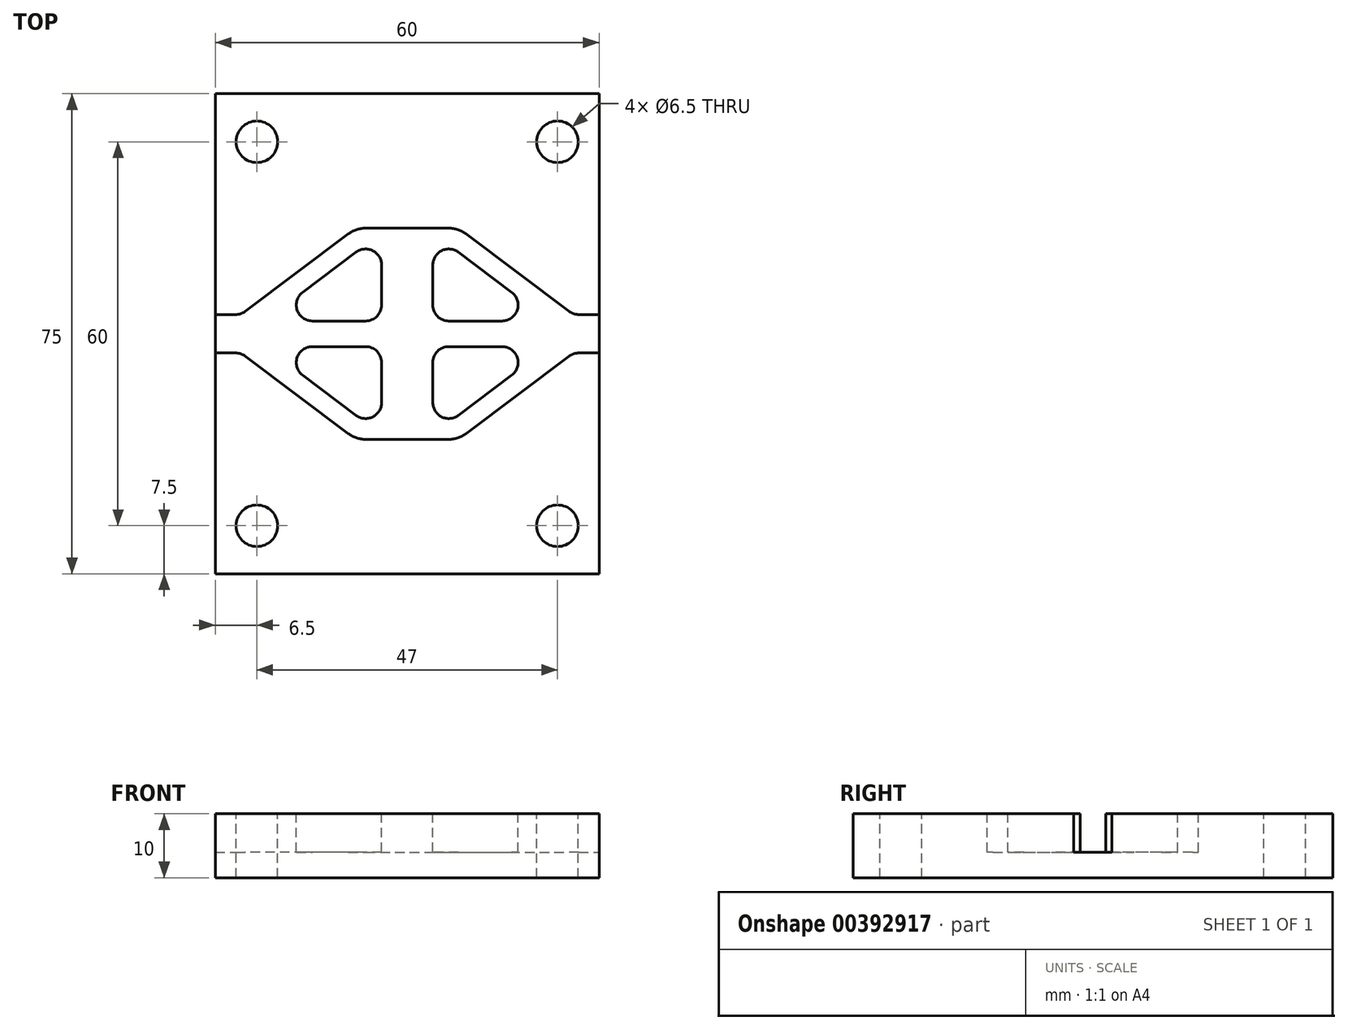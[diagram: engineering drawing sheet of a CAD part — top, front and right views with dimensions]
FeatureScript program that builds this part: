
annotation { "Feature Type Name" : "Feature", "Feature Type Description" : "" }
export const myFeature = defineFeature(function(context is Context, id is Id, definition is map)
    precondition{}
    {
        {
            var Q0;
            Q0=qCreatedBy(makeId("Top.planeOp"),FACE);
            var sketch = newSketch(context, id + "F0", { "sketchPlane" : qUnion([Q0])});
            skLineSegment(sketch, "E0.bottom", {"start": v(-30, 37.5) * mm, "end": v(30, 37.5) * mm});
            skLineSegment(sketch, "E0.top", {"start": v(-30, -37.5) * mm, "end": v(30, -37.5) * mm});
            skLineSegment(sketch, "E0.left", {"start": v(-30, 37.5) * mm, "end": v(-30, -37.5) * mm});
            skLineSegment(sketch, "E0.right", {"start": v(30, 37.5) * mm, "end": v(30, -37.5) * mm});
            skLineSegment(sketch, "E1", {"start": v(0, 76.83) * mm, "end": v(0, -62.83) * mm, "construction": true});
            skLineSegment(sketch, "E2", {"start": v(-62.67, 0) * mm, "end": v(69.33, 0) * mm, "construction": true});
            skLineSegment(sketch, "E3.bottom", {"start": v(-23.5, 30) * mm, "end": v(23.5, 30) * mm, "construction": true});
            skLineSegment(sketch, "E3.top", {"start": v(-23.5, -30) * mm, "end": v(23.5, -30) * mm, "construction": true});
            skLineSegment(sketch, "E3.left", {"start": v(-23.5, 30) * mm, "end": v(-23.5, -30) * mm, "construction": true});
            skLineSegment(sketch, "E3.right", {"start": v(23.5, 30) * mm, "end": v(23.5, -30) * mm, "construction": true});
            skSolve(sketch);
        }
        {
            var Q0;
            Q0=makeQuery(id+"F0.imprint","IMPRINT",FACE,{"disambiguationData":[TD([[makeQuery(id+"F0.imprint","IMPRINT",EDGE,{"derivedFrom":sQuery(id+"F0.wireOp",EDGE,"E0.bottom")}),-1.0]])]});
            extrude(context, id + "F1", {"entities" : qUnion([Q0]), "oppositeDirection" : true, "depth" : 10 * mm});
        }
        {
            var Q0;
            Q0=qCreatedBy(makeId("Top.planeOp"),FACE);
            var sketch = newSketch(context, id + "F2", { "sketchPlane" : qUnion([Q0])});
            skCircle(sketch, "E4", {"center": v(-23.5, 30) * mm, "radius": 3.25 * mm});
            skCircle(sketch, "E5.MirrorC", {"center": v(23.5, 30) * mm, "radius": 3.25 * mm});
            skCircle(sketch, "E6.MirrorC", {"center": v(-23.5, -30) * mm, "radius": 3.25 * mm});
            skCircle(sketch, "E7.MirrorC", {"center": v(23.5, -30) * mm, "radius": 3.25 * mm});
            skSolve(sketch);
        }
        {
            var Q0;
            Q0=qSketchRegion(id+"F2",true);
            extrude(context, id + "F3", {"entities" : qUnion([Q0]), "operationType" : NewBodyOperationType.REMOVE, "endBound" : BoundingType.THROUGH_ALL, "oppositeDirection" : true, "depth" : 25.4 * mm});
        }
        {
            var Q0;
            Q0=makeQuery(id+"F0.imprint","IMPRINT",FACE,{"disambiguationData":[TD([[makeQuery(id+"F0.imprint","IMPRINT",EDGE,{"derivedFrom":sQuery(id+"F0.wireOp",EDGE,"E0.bottom")}),-1.0]])]});
            var sketch = newSketch(context, id + "F4", { "sketchPlane" : qUnion([Q0])});
            skLineSegment(sketch, "E8", {"start": v(-30, 0) * mm, "end": v(-30, 3) * mm});
            skLineSegment(sketch, "E9", {"start": v(-30, 3) * mm, "end": v(4.5, 3) * mm});
            skLineSegment(sketch, "E10", {"start": v(30, 3) * mm, "end": v(30, 0) * mm});
            skLineSegment(sketch, "E11.MirrorCS", {"start": v(-30, -3) * mm, "end": v(30, -3) * mm});
            skLineSegment(sketch, "E12.MirrorCS", {"start": v(-30, 0) * mm, "end": v(-30, -3) * mm});
            skLineSegment(sketch, "E13.MirrorCS", {"start": v(30, -3) * mm, "end": v(30, 0) * mm});
            skLineSegment(sketch, "E14", {"start": v(4, 10.75) * mm, "end": v(4, 4.5) * mm});
            skLineSegment(sketch, "E15", {"start": v(6.5, 2) * mm, "end": v(14.83, 2) * mm});
            skLineSegment(sketch, "E16", {"start": v(8, 12.75) * mm, "end": v(16.33, 6.5) * mm});
            skPoint(sketch, "E17.centerSnap0", {"position": v(4, 8.88) * mm});
            skArc(sketch, "E18", {"start": v(4, 4.5) * mm, "mid": v(4.73, 2.73) * mm, "end": v(6.5, 2) * mm});
            skArc(sketch, "E19", {"start": v(8, 12.75) * mm, "mid": v(5.38, 12.99) * mm, "end": v(4, 10.75) * mm});
            skArc(sketch, "E20", {"start": v(14.83, 2) * mm, "mid": v(17.2, 3.7) * mm, "end": v(16.33, 6.5) * mm});
            skPoint(sketch, "E21.orphan", {"position": v(4, 2) * mm});
            skPoint(sketch, "E22.orphan", {"position": v(4, 15.75) * mm});
            skLineSegment(sketch, "E23.trimOffspring", {"start": v(26, 3) * mm, "end": v(30, 3) * mm});
            skLineSegment(sketch, "E24.0", {"start": v(6.5, 0) * mm, "end": v(16.5, 0) * mm});
            skLineSegment(sketch, "E24.1", {"start": v(9.2, 15.6) * mm, "end": v(19.2, 8.1) * mm});
            skArc(sketch, "E24.2", {"start": v(9.2, 15.6) * mm, "mid": v(7.92, 16.27) * mm, "end": v(6.5, 16.5) * mm});
            skArc(sketch, "E24.5", {"start": v(2, 4.5) * mm, "mid": v(2.06, 3.74) * mm, "end": v(2.26, 3) * mm});
            skLineSegment(sketch, "E25", {"start": v(6.5, 16.5) * mm, "end": v(0, 16.5) * mm});
            skLineSegment(sketch, "E26", {"start": v(19.2, 8.1) * mm, "end": v(26, 3) * mm});
            skArc(sketch, "E27", {"start": v(25.33, 3.5) * mm, "mid": v(26.04, 3.13) * mm, "end": v(26.83, 3) * mm});
            skLineSegment(sketch, "E28.trimOffspring", {"start": v(26.83, 3) * mm, "end": v(30, 3) * mm});
            skLineSegment(sketch, "E29.MirrorCS", {"start": v(6.5, -16.5) * mm, "end": v(0, -16.5) * mm});
            skLineSegment(sketch, "E30.MirrorCS", {"start": v(26, -3) * mm, "end": v(30, -3) * mm});
            skLineSegment(sketch, "E31.MirrorCS", {"start": v(26.83, -3) * mm, "end": v(30, -3) * mm});
            skArc(sketch, "E32.MirrorCS", {"start": v(4, -4.5) * mm, "mid": v(4.73, -2.73) * mm, "end": v(6.5, -2) * mm});
            skArc(sketch, "E33.MirrorCS", {"start": v(25.33, -3.5) * mm, "mid": v(26.04, -3.13) * mm, "end": v(26.83, -3) * mm});
            skArc(sketch, "E34.MirrorCS", {"start": v(2, -4.5) * mm, "mid": v(2.06, -3.74) * mm, "end": v(2.26, -3) * mm});
            skArc(sketch, "E35.MirrorCS", {"start": v(9.2, -15.6) * mm, "mid": v(7.92, -16.27) * mm, "end": v(6.5, -16.5) * mm});
            skArc(sketch, "E36.MirrorCS", {"start": v(8, -12.75) * mm, "mid": v(5.38, -12.99) * mm, "end": v(4, -10.75) * mm});
            skLineSegment(sketch, "E37.MirrorCS", {"start": v(4, -10.75) * mm, "end": v(4, -4.5) * mm});
            skPoint(sketch, "E38.MirrorP", {"position": v(4, -15.75) * mm});
            skPoint(sketch, "E39.MirrorP", {"position": v(4, -8.88) * mm});
            skArc(sketch, "E40.MirrorCS", {"start": v(14.83, -2) * mm, "mid": v(17.2, -3.7) * mm, "end": v(16.33, -6.5) * mm});
            skLineSegment(sketch, "E41.MirrorCS", {"start": v(8, -12.75) * mm, "end": v(16.33, -6.5) * mm});
            skLineSegment(sketch, "E42.MirrorCS", {"start": v(6.5, -2) * mm, "end": v(14.83, -2) * mm});
            skPoint(sketch, "E43.MirrorP", {"position": v(4, -2) * mm});
            skLineSegment(sketch, "E44.MirrorCS", {"start": v(19.2, -8.1) * mm, "end": v(26, -3) * mm});
            skLineSegment(sketch, "E45.MirrorCS", {"start": v(9.2, -15.6) * mm, "end": v(19.2, -8.1) * mm});
            skLineSegment(sketch, "E46.MirrorCS", {"start": v(-26, -3) * mm, "end": v(-30, -3) * mm});
            skLineSegment(sketch, "E47.MirrorCS", {"start": v(-26, 3) * mm, "end": v(-30, 3) * mm});
            skArc(sketch, "E48.MirrorCS", {"start": v(-4, 4.5) * mm, "mid": v(-4.73, 2.73) * mm, "end": v(-6.5, 2) * mm});
            skLineSegment(sketch, "E49.MirrorCS", {"start": v(-26.83, -3) * mm, "end": v(-30, -3) * mm});
            skArc(sketch, "E50.MirrorCS", {"start": v(-25.33, 3.5) * mm, "mid": v(-26.04, 3.13) * mm, "end": v(-26.83, 3) * mm});
            skLineSegment(sketch, "E51.MirrorCS", {"start": v(-26.83, 3) * mm, "end": v(-30, 3) * mm});
            skArc(sketch, "E52.MirrorCS", {"start": v(-25.33, -3.5) * mm, "mid": v(-26.04, -3.13) * mm, "end": v(-26.83, -3) * mm});
            skArc(sketch, "E53.MirrorCS", {"start": v(-4, -4.5) * mm, "mid": v(-4.73, -2.73) * mm, "end": v(-6.5, -2) * mm});
            skArc(sketch, "E54.MirrorCS", {"start": v(-2, -4.5) * mm, "mid": v(-2.06, -3.74) * mm, "end": v(-2.26, -3) * mm});
            skLineSegment(sketch, "E55.MirrorCS", {"start": v(-30, 3) * mm, "end": v(-30, 0) * mm});
            skArc(sketch, "E56.MirrorCS", {"start": v(-2, 4.5) * mm, "mid": v(-2.06, 3.74) * mm, "end": v(-2.26, 3) * mm});
            skArc(sketch, "E57.MirrorCS", {"start": v(-8, -12.75) * mm, "mid": v(-5.38, -12.99) * mm, "end": v(-4, -10.75) * mm});
            skLineSegment(sketch, "E58.MirrorCS", {"start": v(-30, -3) * mm, "end": v(-30, 0) * mm});
            skArc(sketch, "E59.MirrorCS", {"start": v(-8, 12.75) * mm, "mid": v(-5.38, 12.99) * mm, "end": v(-4, 10.75) * mm});
            skArc(sketch, "E60.MirrorCS", {"start": v(-9.2, -15.6) * mm, "mid": v(-7.92, -16.27) * mm, "end": v(-6.5, -16.5) * mm});
            skArc(sketch, "E61.MirrorCS", {"start": v(-9.2, 15.6) * mm, "mid": v(-7.92, 16.27) * mm, "end": v(-6.5, 16.5) * mm});
            skArc(sketch, "E62.MirrorCS", {"start": v(-14.83, -2) * mm, "mid": v(-17.2, -3.7) * mm, "end": v(-16.33, -6.5) * mm});
            skArc(sketch, "E63.MirrorCS", {"start": v(-14.83, 2) * mm, "mid": v(-17.2, 3.7) * mm, "end": v(-16.33, 6.5) * mm});
            skLineSegment(sketch, "E64.MirrorCS", {"start": v(-6.5, 16.5) * mm, "end": v(0, 16.5) * mm});
            skLineSegment(sketch, "E65.MirrorCS", {"start": v(-4, 10.75) * mm, "end": v(-4, 4.5) * mm});
            skLineSegment(sketch, "E66.MirrorCS", {"start": v(-19.2, 8.1) * mm, "end": v(-26, 3) * mm});
            skLineSegment(sketch, "E67.MirrorCS", {"start": v(-6.5, -16.5) * mm, "end": v(0, -16.5) * mm});
            skLineSegment(sketch, "E68.MirrorCS", {"start": v(-4, -10.75) * mm, "end": v(-4, -4.5) * mm});
            skPoint(sketch, "E69.MirrorP", {"position": v(-4, -8.88) * mm});
            skLineSegment(sketch, "E70.MirrorCS", {"start": v(-9.2, 15.6) * mm, "end": v(-19.2, 8.1) * mm});
            skLineSegment(sketch, "E71.MirrorCS", {"start": v(-8, -12.75) * mm, "end": v(-16.33, -6.5) * mm});
            skPoint(sketch, "E72.MirrorP", {"position": v(-4, 15.75) * mm});
            skPoint(sketch, "E73.MirrorP", {"position": v(-4, 8.88) * mm});
            skLineSegment(sketch, "E74.MirrorCS", {"start": v(-6.5, 2) * mm, "end": v(-14.83, 2) * mm});
            skLineSegment(sketch, "E75.MirrorCS", {"start": v(-8, 12.75) * mm, "end": v(-16.33, 6.5) * mm});
            skLineSegment(sketch, "E76.MirrorCS", {"start": v(-19.2, -8.1) * mm, "end": v(-26, -3) * mm});
            skPoint(sketch, "E77.MirrorP", {"position": v(-4, -2) * mm});
            skPoint(sketch, "E78.MirrorP", {"position": v(-4, 2) * mm});
            skPoint(sketch, "E79.MirrorP", {"position": v(-4, -15.75) * mm});
            skLineSegment(sketch, "E80.MirrorCS", {"start": v(-9.2, -15.6) * mm, "end": v(-19.2, -8.1) * mm});
            skLineSegment(sketch, "E81.MirrorCS", {"start": v(-6.5, 0) * mm, "end": v(-16.5, 0) * mm});
            skLineSegment(sketch, "E82.MirrorCS", {"start": v(-6.5, -2) * mm, "end": v(-14.83, -2) * mm});
            skSolve(sketch);
        }
        {
            var Q0;
            Q0 = qSketchRegion(id + "F4", true);
            extrude(context, id + "F5", {"entities" : qUnion([Q0]), "operationType" : NewBodyOperationType.REMOVE, "oppositeDirection" : true, "depth" : 6 * mm});
        }
    });
